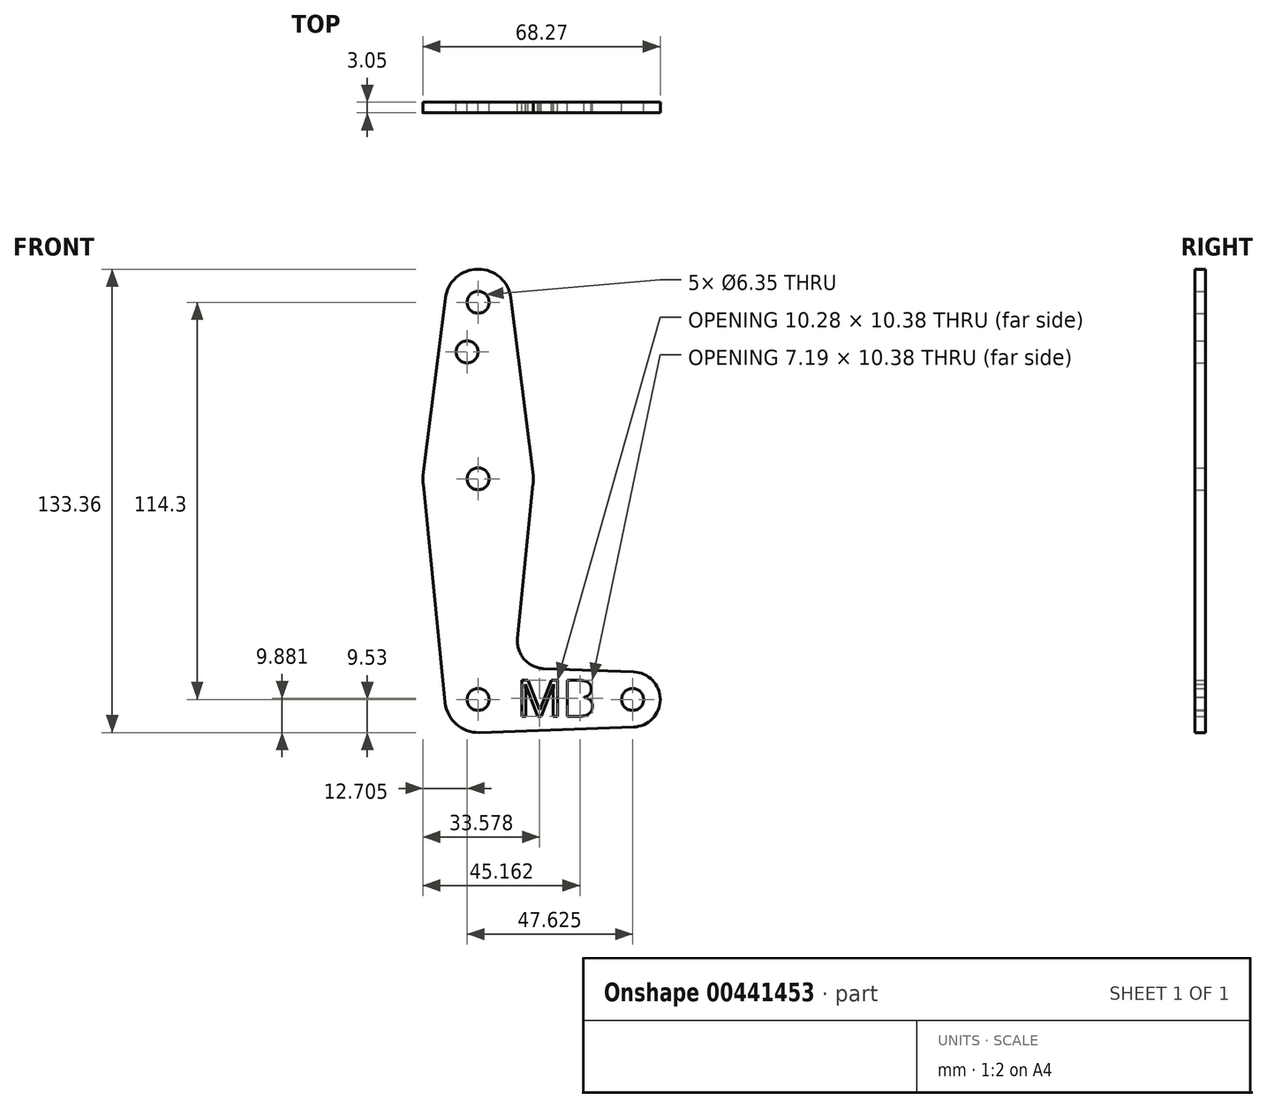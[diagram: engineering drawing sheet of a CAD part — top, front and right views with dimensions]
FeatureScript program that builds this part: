
annotation { "Feature Type Name" : "Feature", "Feature Type Description" : "" }
export const myFeature = defineFeature(function(context is Context, id is Id, definition is map)
    precondition{}
    {
        {
            var Q0;
            Q0=qCreatedBy(makeId("Front.planeOp"),FACE);
            var sketch = newSketch(context, id + "F0", { "sketchPlane" : qUnion([Q0])});
            skLineSegment(sketch, "E0", {"start": v(0, 0) * mm, "end": v(44.45, 0) * mm, "construction": true});
            skLineSegment(sketch, "E1", {"start": v(0, 0) * mm, "end": v(0, 114.3) * mm, "construction": true});
            skCircle(sketch, "E2", {"center": v(44.45, 0) * mm, "radius": 7.94 * mm});
            skCircle(sketch, "E3", {"center": v(0, 0) * mm, "radius": 9.52 * mm});
            skCircle(sketch, "E4", {"center": v(0, 114.3) * mm, "radius": 9.53 * mm});
            skCircle(sketch, "E5", {"center": v(0, 63.5) * mm, "radius": 15.88 * mm});
            skLineSegment(sketch, "E6", {"start": v(0, 0) * mm, "end": v(0, 63.5) * mm, "construction": true});
            skLineSegment(sketch, "E7", {"start": v(-9.45, 115.5) * mm, "end": v(-15.75, 65.48) * mm});
            skLineSegment(sketch, "E8", {"start": v(9.45, 115.5) * mm, "end": v(15.75, 65.48) * mm});
            skLineSegment(sketch, "E9", {"start": v(0.34, -9.52) * mm, "end": v(44.73, -7.93) * mm});
            skCircle(sketch, "E10", {"center": v(0, 114.3) * mm, "radius": 3.18 * mm});
            skCircle(sketch, "E11", {"center": v(0, 63.5) * mm, "radius": 3.18 * mm});
            skCircle(sketch, "E12", {"center": v(0, 0) * mm, "radius": 3.18 * mm});
            skCircle(sketch, "E13", {"center": v(44.45, 0) * mm, "radius": 3.18 * mm});
            skLineSegment(sketch, "E14", {"start": v(0, 63.5) * mm, "end": v(0, 100.03) * mm, "construction": true});
            skCircle(sketch, "E15", {"center": v(-3.18, 100.03) * mm, "radius": 3.18 * mm});
            skLineSegment(sketch, "E16", {"start": v(-3.18, 100.03) * mm, "end": v(0, 100.03) * mm, "construction": true});
            skLineSegment(sketch, "E17", {"start": v(15.8, 61.91) * mm, "end": v(11.34, 17.6) * mm});
            skLineSegment(sketch, "E18", {"start": v(18.97, 8.85) * mm, "end": v(44.73, 7.93) * mm});
            skArc(sketch, "E19.filletArc", {"start": v(11.34, 17.6) * mm, "mid": v(13.26, 11.57) * mm, "end": v(18.97, 8.85) * mm});
            skLineSegment(sketch, "E20", {"start": v(-15.8, 61.91) * mm, "end": v(-9.48, -0.95) * mm});
            skPoint(sketch, "E21.secondSnap0", {"position": v(0, 31.75) * mm});
            skText(sketch, "E22", { "text": "MB", "fontName": "OpenSans-Regular.ttf"});
            const initialGuessF0  = {"E22": [0.01113, -0.00484, 1, 0, 0.01047]};
            skSetInitialGuess(sketch, initialGuessF0);
            skSolve(sketch);
        }
        {
            var Q0;
            Q0=makeQuery(id+"F0.imprint","IMPRINT",FACE,{"disambiguationData":[TD([[makeQuery(id+"F0.imprint","IMPRINT",EDGE,{"derivedFrom":sQuery(id+"F0.wireOp",EDGE,"E13")}),-1.0]])]});
            var Q1;
            Q1=makeQuery(id+"F0.imprint","IMPRINT",FACE,{"disambiguationData":[TD([[makeQuery(id+"F0.imprint","IMPRINT",EDGE,{"derivedFrom":sQuery(id+"F0.wireOp",EDGE,"E12")}),-1.0]])]});
            var Q2;
            Q2=makeQuery(id+"F0.imprint","IMPRINT",FACE,{"disambiguationData":[TD([[makeQuery(id+"F0.imprint","IMPRINT",EDGE,{"derivedFrom":sQuery(id+"F0.wireOp",EDGE,"E10")}),-1.0]])]});
            var Q3;
            {var subQ1=sQuery(id+"F0.wireOp",EDGE,"E7");Q3=makeQuery(id+"F0.imprint","IMPRINT",FACE,{"disambiguationData":[TD([[makeQuery(id+"F0.imprint","IMPRINT",EDGE,{"derivedFrom":subQ1}),1.0]])]});}
            var Q4;
            Q4=makeQuery(id+"F0.imprint","IMPRINT",FACE,{"disambiguationData":[TD([[makeQuery(id+"F0.imprint","IMPRINT",EDGE,{"derivedFrom":sQuery(id+"F0.wireOp",EDGE,"E11")}),-1.0]])]});
            var Q5;
            {var subQ0=sQuery(id+"F0.wireOp",EDGE,"E9");Q5=makeQuery(id+"F0.imprint","IMPRINT",FACE,{"disambiguationData":[TD([[makeQuery(id+"F0.imprint","IMPRINT",EDGE,{"derivedFrom":subQ0}),1.0]])]});}
            extrude(context, id + "F1", {"entities" : qUnion([Q0, Q1, Q2, Q3, Q4, Q5]), "depth" : 3.05 * mm});
        }
    });
